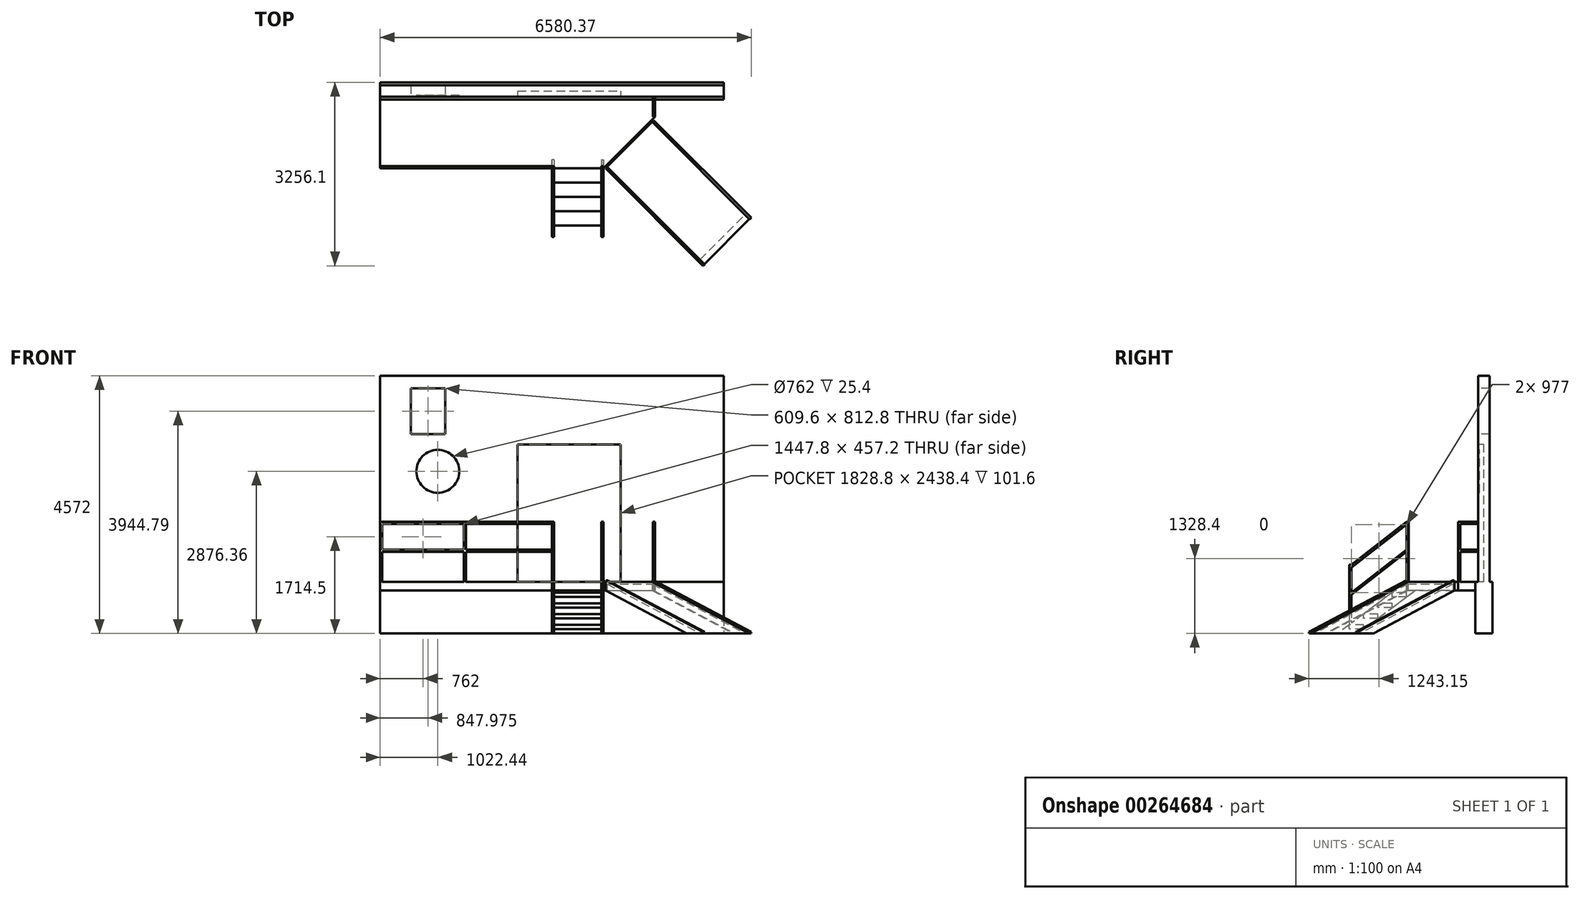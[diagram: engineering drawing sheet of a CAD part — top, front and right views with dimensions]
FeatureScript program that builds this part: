
annotation { "Feature Type Name" : "Feature", "Feature Type Description" : "" }
export const myFeature = defineFeature(function(context is Context, id is Id, definition is map)
    precondition{}
    {
        {
            var Q0;
            Q0=qCreatedBy(makeId("Top.planeOp"),FACE);
            var sketch = newSketch(context, id + "F0", { "sketchPlane" : qUnion([Q0])});
            skLineSegment(sketch, "E0.bottom", {"start": v(-3048, 152.4) * mm, "end": v(3048, 152.4) * mm});
            skLineSegment(sketch, "E0.top", {"start": v(-3048, -152.4) * mm, "end": v(3048, -152.4) * mm});
            skLineSegment(sketch, "E0.left", {"start": v(-3048, 152.4) * mm, "end": v(-3048, -152.4) * mm});
            skLineSegment(sketch, "E0.right", {"start": v(3048, 152.4) * mm, "end": v(3048, -152.4) * mm});
            skPoint(sketch, "E0.middle", {"position": v(0, 0) * mm});
            skSolve(sketch);
        }
        {
            var Q0;
            Q0=makeQuery(id+"F0.imprint","IMPRINT",FACE,{"disambiguationData":[TD([[makeQuery(id+"F0.imprint","IMPRINT",EDGE,{"derivedFrom":sQuery(id+"F0.wireOp",EDGE,"E0.bottom")}),-1.0]])]});
            extrude(context, id + "F1", {"entities" : qUnion([Q0]), "depth" : 914.4 * mm});
        }
        {
            var Q0;
            Q0=qCreatedBy(makeId("Front.planeOp"),FACE);
            var sketch = newSketch(context, id + "F2", { "sketchPlane" : qUnion([Q0])});
            skLineSegment(sketch, "E1.0", {"start": v(-3048, 914.4) * mm, "end": v(3048, 914.4) * mm});
            skLineSegment(sketch, "E2", {"start": v(-3048, 914.4) * mm, "end": v(-3048, 4572) * mm});
            skLineSegment(sketch, "E3", {"start": v(-3048, 4572) * mm, "end": v(3048, 4572) * mm});
            skLineSegment(sketch, "E4", {"start": v(3048, 4572) * mm, "end": v(3048, 914.4) * mm});
            skSolve(sketch);
        }
        {
            var Q0;
            Q0=makeQuery(id+"F2.imprint","IMPRINT",FACE,{"disambiguationData":[TD([[makeQuery(id+"F2.imprint","IMPRINT",EDGE,{"derivedFrom":sQuery(id+"F2.wireOp",EDGE,"E1.0")}),1.0]])]});
            extrude(context, id + "F3", {"entities" : qUnion([Q0]), "operationType" : NewBodyOperationType.ADD, "endBound" : BoundingType.SYMMETRIC, "depth" : 203.2 * mm});
        }
        {
            var Q0;
            Q0=makeQuery(id+"F3.boolean.opBoolean","MERGE",FACE,{"derivedFrom":[makeQuery(id+"F1.opExtrude","SWEPT_FACE",FACE,{"disambiguationData":[OSD([sQuery(id+"F0.wireOp",EDGE,"E0.right")])]}),makeQuery(id+"F3.opExtrude","SWEPT_FACE",FACE,{"disambiguationData":[OSD([sQuery(id+"F2.wireOp",EDGE,"E4")])]})]});
            cPlane(context, id + "F4", {"entities" : qUnion([Q0]), "cplaneType" : CPlaneType.OFFSET, "offset" : 1219.2 * mm, "oppositeDirection" : true, "width" : 152.4 * mm, "height" : 152.4 * mm});
        }
        {
            var Q0;
            Q0=qCreatedBy(id+"F4.planeOp",FACE);
            var sketch = newSketch(context, id + "F5", { "sketchPlane" : qUnion([Q0])});
            skPoint(sketch, "E5.0", {"position": v(-152.4, 914.4) * mm});
            skLineSegment(sketch, "E6.bottom", {"start": v(-152.4, 914.4) * mm, "end": v(-1371.6, 914.4) * mm});
            skLineSegment(sketch, "E6.top", {"start": v(-152.4, 762) * mm, "end": v(-1371.6, 762) * mm});
            skLineSegment(sketch, "E6.left", {"start": v(-152.4, 914.4) * mm, "end": v(-152.4, 762) * mm});
            skLineSegment(sketch, "E6.right", {"start": v(-1371.6, 914.4) * mm, "end": v(-1371.6, 762) * mm});
            skSolve(sketch);
        }
        {
            var Q0;
            Q0=makeQuery(id+"F5.imprint","IMPRINT",FACE,{"disambiguationData":[TD([[makeQuery(id+"F5.imprint","IMPRINT",EDGE,{"derivedFrom":sQuery(id+"F5.wireOp",EDGE,"E6.bottom")}),1.0]])]});
            extrude(context, id + "F6", {"entities" : qUnion([Q0]), "oppositeDirection" : true, "depth" : 4876.8 * mm});
        }
        {
            var Q0;
            Q0=makeQuery(id+"F3.opExtrude","CAP_FACE",FACE,{"disambiguationData":[OSD([sQuery(id+"F2.wireOp",EDGE,"E1.0"),sQuery(id+"F2.wireOp",EDGE,"E2"),sQuery(id+"F2.wireOp",EDGE,"E3"),sQuery(id+"F2.wireOp",EDGE,"E4")])],"isStart":false});
            var sketch = newSketch(context, id + "F7", { "sketchPlane" : qUnion([Q0])});
            skLineSegment(sketch, "E7.bottom", {"start": v(1219.2, 914.4) * mm, "end": v(-609.6, 914.4) * mm});
            skLineSegment(sketch, "E7.top", {"start": v(1219.2, 3352.8) * mm, "end": v(-609.6, 3352.8) * mm});
            skLineSegment(sketch, "E7.left", {"start": v(1219.2, 914.4) * mm, "end": v(1219.2, 3352.8) * mm});
            skLineSegment(sketch, "E7.right", {"start": v(-609.6, 914.4) * mm, "end": v(-609.6, 3352.8) * mm});
            skSolve(sketch);
        }
        {
            var Q0;
            Q0=makeQuery(id+"F7.imprint","IMPRINT",FACE,{"disambiguationData":[TD([[makeQuery(id+"F7.imprint","IMPRINT",EDGE,{"derivedFrom":sQuery(id+"F7.wireOp",EDGE,"E7.bottom")}),1.0]])]});
            extrude(context, id + "F8", {"entities" : qUnion([Q0]), "operationType" : NewBodyOperationType.REMOVE, "oppositeDirection" : true, "depth" : 101.6 * mm});
        }
        {
            var Q0;
            Q0=makeQuery(id+"F6.opExtrude","CAP_EDGE",EDGE,{"disambiguationData":[OSD([sQuery(id+"F5.wireOp",EDGE,"E6.right")])],"isStart":true});
            chamfer(context, id + "F9", {"entities" : qUnion([Q0]), "width" : 914.4 * mm, "tangentPropagation" : true});
        }
        {
            var Q0;
            {var subQ0=sQuery(id+"F5.wireOp",EDGE,"E6.right");Q0=makeQuery(id+"F9.opChamfer","BLEND_EDGE",EDGE,{"blendedFrom":[makeQuery(id+"F6.opExtrude","CAP_EDGE",EDGE,{"disambiguationData":[OSD([subQ0])],"isStart":true}),makeQuery(id+"F6.opExtrude","SWEPT_FACE",FACE,{"disambiguationData":[OSD([subQ0])]})],"blendedInto":[makeQuery(id+"F6.opExtrude","SWEPT_FACE",FACE,{"disambiguationData":[OSD([subQ0])]})]});}
            cPoint(context, id + "F10", {"entities" : qUnion([Q0]), "parameter" : 0.5});
        }
        {
            var Q0;
            Q0=qCreatedBy(id+"F4.planeOp",FACE);
            var Q1;
            Q1 = qCreatedBy(id + "F10" ,VERTEX);
            cPlane(context, id + "F11", {"entities" : qUnion([Q0, Q1]), "cplaneType" : CPlaneType.PLANE_POINT, "offset" : 25.4 * mm, "width" : 152.4 * mm, "height" : 152.4 * mm});
        }
        {
            var Q0;
            Q0=qCreatedBy(id+"F11.planeOp",FACE);
            var sketch = newSketch(context, id + "F12", { "sketchPlane" : qUnion([Q0])});
            skLineSegment(sketch, "E8.0", {"start": v(-1371.6, 914.4) * mm, "end": v(-152.4, 914.4) * mm});
            skLineSegment(sketch, "E9.0", {"start": v(-457.2, 762) * mm, "end": v(-1371.6, 762) * mm});
            skLineSegment(sketch, "E10", {"start": v(-1371.6, 914.4) * mm, "end": v(-2590.8, 0) * mm});
            skLineSegment(sketch, "E11", {"start": v(-2590.8, 0) * mm, "end": v(-2235.2, 0) * mm});
            skLineSegment(sketch, "E12", {"start": v(-2235.2, 0) * mm, "end": v(-1219.2, 762) * mm});
            skLineSegment(sketch, "E13", {"start": v(-1219.2, 762) * mm, "end": v(-1371.6, 762) * mm});
            skLineSegment(sketch, "E14.bottom", {"start": v(-1371.6, 647.7) * mm, "end": v(-1625.6, 647.7) * mm});
            skLineSegment(sketch, "E14.top", {"start": v(-1371.6, 723.9) * mm, "end": v(-1625.6, 723.9) * mm});
            skLineSegment(sketch, "E14.left", {"start": v(-1371.6, 647.7) * mm, "end": v(-1371.6, 723.9) * mm});
            skLineSegment(sketch, "E14.right", {"start": v(-1625.6, 647.7) * mm, "end": v(-1625.6, 723.9) * mm});
            skLineSegment(sketch, "E15.bottom", {"start": v(-1625.6, 457.2) * mm, "end": v(-1879.6, 457.2) * mm});
            skLineSegment(sketch, "E15.top", {"start": v(-1625.6, 533.4) * mm, "end": v(-1879.6, 533.4) * mm});
            skLineSegment(sketch, "E15.left", {"start": v(-1625.6, 457.2) * mm, "end": v(-1625.6, 533.4) * mm});
            skLineSegment(sketch, "E15.right", {"start": v(-1879.6, 457.2) * mm, "end": v(-1879.6, 533.4) * mm});
            skLineSegment(sketch, "E16.bottom", {"start": v(-1879.6, 266.7) * mm, "end": v(-2133.6, 266.7) * mm});
            skLineSegment(sketch, "E16.top", {"start": v(-1879.6, 342.9) * mm, "end": v(-2133.6, 342.9) * mm});
            skLineSegment(sketch, "E16.left", {"start": v(-1879.6, 266.7) * mm, "end": v(-1879.6, 342.9) * mm});
            skLineSegment(sketch, "E16.right", {"start": v(-2133.6, 266.7) * mm, "end": v(-2133.6, 342.9) * mm});
            skLineSegment(sketch, "E17.bottom", {"start": v(-2133.6, 76.2) * mm, "end": v(-2387.6, 76.2) * mm});
            skLineSegment(sketch, "E17.top", {"start": v(-2133.6, 152.4) * mm, "end": v(-2387.6, 152.4) * mm});
            skLineSegment(sketch, "E17.left", {"start": v(-2133.6, 76.2) * mm, "end": v(-2133.6, 152.4) * mm});
            skLineSegment(sketch, "E17.right", {"start": v(-2387.6, 76.2) * mm, "end": v(-2387.6, 152.4) * mm});
            skLineSegment(sketch, "E18", {"start": v(-1371.6, 762) * mm, "end": v(-1219.2, 762) * mm});
            skLineSegment(sketch, "E19", {"start": v(-1371.6, 762) * mm, "end": v(-1371.6, 914.4) * mm});
            skSolve(sketch);
        }
        {
            var Q0;
            {var subQ1=sQuery(id+"F12.wireOp",EDGE,"E11");Q0=makeQuery(id+"F12.imprint","IMPRINT",FACE,{"disambiguationData":[TD([[makeQuery(id+"F12.imprint","IMPRINT",EDGE,{"derivedFrom":subQ1}),1.0]])]});}
            var Q1;
            Q1=makeQuery(id+"F12.imprint","IMPRINT",FACE,{"disambiguationData":[TD([[makeQuery(id+"F12.imprint","IMPRINT",EDGE,{"derivedFrom":sQuery(id+"F12.wireOp",EDGE,"E17.bottom")}),-1.0]])]});
            var Q2;
            {var subQ1=sQuery(id+"F12.wireOp",EDGE,"E16.bottom");Q2=makeQuery(id+"F12.imprint","IMPRINT",FACE,{"disambiguationData":[TD([[makeQuery(id+"F12.imprint","IMPRINT",EDGE,{"derivedFrom":subQ1}),1.0]])]});}
            var Q3;
            Q3=makeQuery(id+"F12.imprint","IMPRINT",FACE,{"disambiguationData":[TD([[makeQuery(id+"F12.imprint","IMPRINT",EDGE,{"derivedFrom":sQuery(id+"F12.wireOp",EDGE,"E16.bottom")}),-1.0]])]});
            var Q4;
            {var subQ1=sQuery(id+"F12.wireOp",EDGE,"E15.bottom");Q4=makeQuery(id+"F12.imprint","IMPRINT",FACE,{"disambiguationData":[TD([[makeQuery(id+"F12.imprint","IMPRINT",EDGE,{"derivedFrom":subQ1}),1.0]])]});}
            var Q5;
            Q5=makeQuery(id+"F12.imprint","IMPRINT",FACE,{"disambiguationData":[TD([[makeQuery(id+"F12.imprint","IMPRINT",EDGE,{"derivedFrom":sQuery(id+"F12.wireOp",EDGE,"E15.bottom")}),-1.0]])]});
            var Q6;
            {var subQ1=sQuery(id+"F12.wireOp",EDGE,"E14.bottom");Q6=makeQuery(id+"F12.imprint","IMPRINT",FACE,{"disambiguationData":[TD([[makeQuery(id+"F12.imprint","IMPRINT",EDGE,{"derivedFrom":subQ1}),1.0]])]});}
            var Q7;
            Q7=makeQuery(id+"F12.imprint","IMPRINT",FACE,{"disambiguationData":[TD([[makeQuery(id+"F12.imprint","IMPRINT",EDGE,{"derivedFrom":sQuery(id+"F12.wireOp",EDGE,"E14.bottom")}),-1.0]])]});
            var Q8;
            {var subQ3=sQuery(id+"F12.wireOp",EDGE,"E14.top");Q8=makeQuery(id+"F12.imprint","IMPRINT",FACE,{"disambiguationData":[TD([[makeQuery(id+"F12.imprint","IMPRINT",EDGE,{"derivedFrom":subQ3}),-1.0]])]});}
            extrude(context, id + "F13", {"entities" : qUnion([Q0, Q1, Q2, Q3, Q4, Q5, Q6, Q7, Q8]), "operationType" : NewBodyOperationType.ADD, "oppositeDirection" : true, "depth" : 38.1 * mm});
        }
        {
            var Q0;
            Q0=makeQuery(id+"F12.imprint","IMPRINT",FACE,{"disambiguationData":[TD([[makeQuery(id+"F12.imprint","IMPRINT",EDGE,{"derivedFrom":sQuery(id+"F12.wireOp",EDGE,"E17.bottom")}),-1.0]])]});
            var Q1;
            Q1=makeQuery(id+"F12.imprint","IMPRINT",FACE,{"disambiguationData":[TD([[makeQuery(id+"F12.imprint","IMPRINT",EDGE,{"derivedFrom":sQuery(id+"F12.wireOp",EDGE,"E16.bottom")}),-1.0]])]});
            var Q2;
            Q2=makeQuery(id+"F12.imprint","IMPRINT",FACE,{"disambiguationData":[TD([[makeQuery(id+"F12.imprint","IMPRINT",EDGE,{"derivedFrom":sQuery(id+"F12.wireOp",EDGE,"E15.bottom")}),-1.0]])]});
            var Q3;
            Q3=makeQuery(id+"F12.imprint","IMPRINT",FACE,{"disambiguationData":[TD([[makeQuery(id+"F12.imprint","IMPRINT",EDGE,{"derivedFrom":sQuery(id+"F12.wireOp",EDGE,"E14.bottom")}),-1.0]])]});
            extrude(context, id + "F14", {"entities" : qUnion([Q0, Q1, Q2, Q3]), "operationType" : NewBodyOperationType.ADD, "oppositeDirection" : true, "depth" : 914.4 * mm});
        }
        {
            var Q0;
            Q0=makeQuery(id+"F14.opExtrude","CAP_FACE",FACE,{"disambiguationData":[OSD([sQuery(id+"F12.wireOp",EDGE,"E14.bottom"),sQuery(id+"F12.wireOp",EDGE,"E14.top"),sQuery(id+"F12.wireOp",EDGE,"E14.left"),sQuery(id+"F12.wireOp",EDGE,"E14.right")])],"isStart":false});
            var sketch = newSketch(context, id + "F15", { "sketchPlane" : qUnion([Q0])});
            skLineSegment(sketch, "E20.0", {"start": v(1371.6, 762) * mm, "end": v(1371.6, 914.4) * mm});
            skLineSegment(sketch, "E21.0", {"start": v(1371.6, 914.4) * mm, "end": v(2590.8, 0) * mm});
            skLineSegment(sketch, "E22.0", {"start": v(2235.2, 0) * mm, "end": v(1219.2, 762) * mm});
            skLineSegment(sketch, "E23.0", {"start": v(2590.8, 0) * mm, "end": v(2235.2, 0) * mm});
            skLineSegment(sketch, "E24.0", {"start": v(457.2, 762) * mm, "end": v(1371.6, 762) * mm});
            skSolve(sketch);
        }
        {
            var Q0;
            {var subQ1=sQuery(id+"F15.wireOp",EDGE,"E20.0");Q0=makeQuery(id+"F15.imprint","IMPRINT",FACE,{"disambiguationData":[TD([[makeQuery(id+"F15.imprint","IMPRINT",EDGE,{"derivedFrom":subQ1}),-1.0]])]});}
            var Q1;
            Q1=makeQuery(id+"F15.imprint","IMPRINT",FACE,{"disambiguationData":[TD([[makeQuery(id+"F15.imprint","IMPRINT",EDGE,{"derivedFrom":makeQuery(id+"F14.opExtrude","CAP_EDGE",EDGE,{"disambiguationData":[OSD([sQuery(id+"F12.wireOp",EDGE,"E14.bottom")])],"isStart":false})}),1.0]])]});
            var Q2;
            {var subQ0=sQuery(id+"F15.wireOp",EDGE,"E23.0");Q2=makeQuery(id+"F15.imprint","IMPRINT",FACE,{"disambiguationData":[TD([[makeQuery(id+"F15.imprint","IMPRINT",EDGE,{"derivedFrom":subQ0}),-1.0]])]});}
            extrude(context, id + "F16", {"entities" : qUnion([Q0, Q1, Q2]), "operationType" : NewBodyOperationType.ADD, "oppositeDirection" : true, "depth" : 38.1 * mm});
        }
        {
            var Q0;
            {var subQ2=sQuery(id+"F0.wireOp",EDGE,"E0.right");var subQ3=sQuery(id+"F0.wireOp",EDGE,"E0.left");var subQ4=sQuery(id+"F0.wireOp",EDGE,"E0.top");Q0=makeQuery(id+"F8.boolean.opBoolean","MERGE",FACE,{"derivedFrom":[makeQuery(id+"F6.boolean.opBoolean","MERGE",FACE,{"derivedFrom":[makeQuery(id+"F3.boolean.opBoolean","SPLIT",FACE,{"disambiguationData":[TD([makeQuery(id+"F1.opExtrude","SWEPT_FACE",FACE,{"disambiguationData":[OSD([subQ4])]})])],"derivedFrom":makeQuery(id+"F1.opExtrude","CAP_FACE",FACE,{"disambiguationData":[OSD([sQuery(id+"F0.wireOp",EDGE,"E0.bottom"),subQ4,subQ3,subQ2])],"isStart":false})}),makeQuery(id+"F6.opExtrude","SWEPT_FACE",FACE,{"disambiguationData":[OSD([sQuery(id+"F5.wireOp",EDGE,"E6.bottom")])]})]}),makeQuery(id+"F8.opExtrude","SWEPT_FACE",FACE,{"disambiguationData":[OSD([sQuery(id+"F7.wireOp",EDGE,"E7.bottom")])]})]});}
            var sketch = newSketch(context, id + "F17", { "sketchPlane" : qUnion([Q0])});
            skLineSegment(sketch, "E25.bottom", {"start": v(-3048, -1371.6) * mm, "end": v(-3009.9, -1371.6) * mm});
            skLineSegment(sketch, "E25.top", {"start": v(-3048, -1333.5) * mm, "end": v(-3009.9, -1333.5) * mm});
            skLineSegment(sketch, "E25.left", {"start": v(-3048, -1371.6) * mm, "end": v(-3048, -1333.5) * mm});
            skLineSegment(sketch, "E25.right", {"start": v(-3009.9, -1371.6) * mm, "end": v(-3009.9, -1333.5) * mm});
            skLineSegment(sketch, "E26.bottom", {"start": v(0, -1371.6) * mm, "end": v(38.1, -1371.6) * mm});
            skLineSegment(sketch, "E26.top", {"start": v(0, -1333.5) * mm, "end": v(38.1, -1333.5) * mm});
            skLineSegment(sketch, "E26.left", {"start": v(0, -1371.6) * mm, "end": v(0, -1333.5) * mm});
            skLineSegment(sketch, "E26.right", {"start": v(38.1, -1371.6) * mm, "end": v(38.1, -1333.5) * mm});
            skLineSegment(sketch, "E27.bottom", {"start": v(914.4, -1371.6) * mm, "end": v(876.3, -1371.6) * mm});
            skLineSegment(sketch, "E27.top", {"start": v(914.4, -1333.5) * mm, "end": v(876.3, -1333.5) * mm});
            skLineSegment(sketch, "E27.left", {"start": v(914.4, -1371.6) * mm, "end": v(914.4, -1333.5) * mm});
            skLineSegment(sketch, "E27.right", {"start": v(876.3, -1371.6) * mm, "end": v(876.3, -1333.5) * mm});
            skLineSegment(sketch, "E28.bottom", {"start": v(1828.8, -457.2) * mm, "end": v(1790.7, -457.2) * mm});
            skLineSegment(sketch, "E28.top", {"start": v(1828.8, -419.1) * mm, "end": v(1790.7, -419.1) * mm});
            skLineSegment(sketch, "E28.left", {"start": v(1828.8, -457.2) * mm, "end": v(1828.8, -419.1) * mm});
            skLineSegment(sketch, "E28.right", {"start": v(1790.7, -457.2) * mm, "end": v(1790.7, -419.1) * mm});
            skLineSegment(sketch, "E29.bottom", {"start": v(-1562.1, -1371.6) * mm, "end": v(-1524, -1371.6) * mm});
            skLineSegment(sketch, "E29.top", {"start": v(-1562.1, -1333.5) * mm, "end": v(-1524, -1333.5) * mm});
            skLineSegment(sketch, "E29.left", {"start": v(-1562.1, -1371.6) * mm, "end": v(-1562.1, -1333.5) * mm});
            skLineSegment(sketch, "E29.right", {"start": v(-1524, -1371.6) * mm, "end": v(-1524, -1333.5) * mm});
            skSolve(sketch);
        }
        {
            var Q0;
            Q0=makeQuery(id+"F17.imprint","IMPRINT",FACE,{"disambiguationData":[TD([[makeQuery(id+"F17.imprint","IMPRINT",EDGE,{"derivedFrom":sQuery(id+"F17.wireOp",EDGE,"E25.bottom")}),1.0]])]});
            var Q1;
            Q1=makeQuery(id+"F17.imprint","IMPRINT",FACE,{"disambiguationData":[TD([[makeQuery(id+"F17.imprint","IMPRINT",EDGE,{"derivedFrom":sQuery(id+"F17.wireOp",EDGE,"E29.bottom")}),1.0]])]});
            var Q2;
            Q2=makeQuery(id+"F17.imprint","IMPRINT",FACE,{"disambiguationData":[TD([[makeQuery(id+"F17.imprint","IMPRINT",EDGE,{"derivedFrom":sQuery(id+"F17.wireOp",EDGE,"E26.bottom")}),-1.0]])]});
            var Q3;
            Q3=makeQuery(id+"F17.imprint","IMPRINT",FACE,{"disambiguationData":[TD([[makeQuery(id+"F17.imprint","IMPRINT",EDGE,{"derivedFrom":sQuery(id+"F17.wireOp",EDGE,"E27.bottom")}),1.0]])]});
            var Q4;
            Q4=makeQuery(id+"F17.imprint","IMPRINT",FACE,{"disambiguationData":[TD([[makeQuery(id+"F17.imprint","IMPRINT",EDGE,{"derivedFrom":sQuery(id+"F17.wireOp",EDGE,"E28.bottom")}),-1.0]])]});
            var Q5;
            Q5=makeQuery(id+"F17.imprint","IMPRINT",FACE,{"disambiguationData":[TD([[makeQuery(id+"F17.imprint","IMPRINT",EDGE,{"derivedFrom":sQuery(id+"F17.wireOp",EDGE,"E26.bottom")}),1.0]])]});
            var Q6;
            Q6=makeQuery(id+"F17.imprint","IMPRINT",FACE,{"disambiguationData":[TD([[makeQuery(id+"F17.imprint","IMPRINT",EDGE,{"derivedFrom":sQuery(id+"F17.wireOp",EDGE,"E27.bottom")}),-1.0]])]});
            extrude(context, id + "F18", {"entities" : qUnion([Q0, Q1, Q2, Q3, Q4, Q5, Q6]), "operationType" : NewBodyOperationType.ADD, "depth" : 1066.8 * mm});
        }
        {
            var Q0;
            Q0=makeQuery(id+"F18.opExtrude","SWEPT_FACE",FACE,{"disambiguationData":[OSD([sQuery(id+"F17.wireOp",EDGE,"E26.left")])]});
            var sketch = newSketch(context, id + "F19", { "sketchPlane" : qUnion([Q0])});
            skLineSegment(sketch, "E30.bottom", {"start": v(1333.5, 1981.2) * mm, "end": v(1371.6, 1981.2) * mm});
            skLineSegment(sketch, "E30.top", {"start": v(1333.5, 1943.1) * mm, "end": v(1371.6, 1943.1) * mm});
            skLineSegment(sketch, "E30.left", {"start": v(1333.5, 1981.2) * mm, "end": v(1333.5, 1943.1) * mm});
            skLineSegment(sketch, "E30.right", {"start": v(1371.6, 1981.2) * mm, "end": v(1371.6, 1943.1) * mm});
            skLineSegment(sketch, "E31.bottom", {"start": v(1371.6, 1447.8) * mm, "end": v(1333.5, 1447.8) * mm});
            skLineSegment(sketch, "E31.top", {"start": v(1371.6, 1485.9) * mm, "end": v(1333.5, 1485.9) * mm});
            skLineSegment(sketch, "E31.left", {"start": v(1371.6, 1447.8) * mm, "end": v(1371.6, 1485.9) * mm});
            skLineSegment(sketch, "E31.right", {"start": v(1333.5, 1447.8) * mm, "end": v(1333.5, 1485.9) * mm});
            skSolve(sketch);
        }
        {
            var Q0;
            Q0=makeQuery(id+"F19.imprint","IMPRINT",FACE,{"disambiguationData":[TD([[makeQuery(id+"F19.imprint","IMPRINT",EDGE,{"derivedFrom":sQuery(id+"F19.wireOp",EDGE,"E30.bottom")}),1.0]])]});
            var Q1;
            Q1=makeQuery(id+"F19.imprint","IMPRINT",FACE,{"disambiguationData":[TD([[makeQuery(id+"F19.imprint","IMPRINT",EDGE,{"derivedFrom":sQuery(id+"F19.wireOp",EDGE,"E31.bottom")}),-1.0]])]});
            var Q2;
            Q2=makeQuery(id+"F18.boolean.opBoolean","MERGE",FACE,{"derivedFrom":[makeQuery(id+"F6.boolean.opBoolean","MERGE",FACE,{"derivedFrom":[makeQuery(id+"F3.boolean.opBoolean","MERGE",FACE,{"derivedFrom":[makeQuery(id+"F1.opExtrude","SWEPT_FACE",FACE,{"disambiguationData":[OSD([sQuery(id+"F0.wireOp",EDGE,"E0.left")])]}),makeQuery(id+"F3.opExtrude","SWEPT_FACE",FACE,{"disambiguationData":[OSD([sQuery(id+"F2.wireOp",EDGE,"E2")])]})]}),makeQuery(id+"F6.opExtrude","CAP_FACE",FACE,{"disambiguationData":[OSD([sQuery(id+"F5.wireOp",EDGE,"E6.bottom"),sQuery(id+"F5.wireOp",EDGE,"E6.top"),sQuery(id+"F5.wireOp",EDGE,"E6.left"),sQuery(id+"F5.wireOp",EDGE,"E6.right")])],"isStart":false})]}),makeQuery(id+"F18.opExtrude","SWEPT_FACE",FACE,{"disambiguationData":[OSD([sQuery(id+"F17.wireOp",EDGE,"E25.left")])]})]});
            extrude(context, id + "F20", {"entities" : qUnion([Q0, Q1]), "operationType" : NewBodyOperationType.ADD, "endBound" : BoundingType.UP_TO_SURFACE, "endBoundEntityFace" : qUnion([Q2]), "depth" : 25.4 * mm});
        }
        {
            var Q0;
            Q0=makeQuery(id+"F18.opExtrude","SWEPT_FACE",FACE,{"disambiguationData":[OSD([sQuery(id+"F17.wireOp",EDGE,"E28.top")])]});
            var sketch = newSketch(context, id + "F21", { "sketchPlane" : qUnion([Q0])});
            skLineSegment(sketch, "E32.bottom", {"start": v(-1828.8, 1981.2) * mm, "end": v(-1790.7, 1981.2) * mm});
            skLineSegment(sketch, "E32.top", {"start": v(-1828.8, 1943.1) * mm, "end": v(-1790.7, 1943.1) * mm});
            skLineSegment(sketch, "E32.left", {"start": v(-1828.8, 1981.2) * mm, "end": v(-1828.8, 1943.1) * mm});
            skLineSegment(sketch, "E32.right", {"start": v(-1790.7, 1981.2) * mm, "end": v(-1790.7, 1943.1) * mm});
            skLineSegment(sketch, "E33.bottom", {"start": v(-1828.8, 1447.8) * mm, "end": v(-1790.7, 1447.8) * mm});
            skLineSegment(sketch, "E33.top", {"start": v(-1828.8, 1485.9) * mm, "end": v(-1790.7, 1485.9) * mm});
            skLineSegment(sketch, "E33.left", {"start": v(-1828.8, 1447.8) * mm, "end": v(-1828.8, 1485.9) * mm});
            skLineSegment(sketch, "E33.right", {"start": v(-1790.7, 1447.8) * mm, "end": v(-1790.7, 1485.9) * mm});
            skSolve(sketch);
        }
        {
            var Q0;
            Q0=makeQuery(id+"F21.imprint","IMPRINT",FACE,{"disambiguationData":[TD([[makeQuery(id+"F21.imprint","IMPRINT",EDGE,{"derivedFrom":sQuery(id+"F21.wireOp",EDGE,"E32.bottom")}),-1.0]])]});
            var Q1;
            Q1=makeQuery(id+"F21.imprint","IMPRINT",FACE,{"disambiguationData":[TD([[makeQuery(id+"F21.imprint","IMPRINT",EDGE,{"derivedFrom":sQuery(id+"F21.wireOp",EDGE,"E33.bottom")}),1.0]])]});
            extrude(context, id + "F22", {"entities" : qUnion([Q0, Q1]), "operationType" : NewBodyOperationType.ADD, "depth" : 304.8 * mm});
        }
        {
            var Q0;
            Q0=makeQuery(id+"F14.opExtrude","SWEPT_FACE",FACE,{"disambiguationData":[OSD([sQuery(id+"F12.wireOp",EDGE,"E17.top")])]});
            var sketch = newSketch(context, id + "F23", { "sketchPlane" : qUnion([Q0])});
            skLineSegment(sketch, "E34.bottom", {"start": v(38.1, -2387.6) * mm, "end": v(0, -2387.6) * mm});
            skLineSegment(sketch, "E34.top", {"start": v(38.1, -2349.5) * mm, "end": v(0, -2349.5) * mm});
            skLineSegment(sketch, "E34.left", {"start": v(38.1, -2387.6) * mm, "end": v(38.1, -2349.5) * mm});
            skLineSegment(sketch, "E34.right", {"start": v(0, -2387.6) * mm, "end": v(0, -2349.5) * mm});
            skLineSegment(sketch, "E35.bottom", {"start": v(876.3, -2387.6) * mm, "end": v(914.4, -2387.6) * mm});
            skLineSegment(sketch, "E35.top", {"start": v(876.3, -2349.5) * mm, "end": v(914.4, -2349.5) * mm});
            skLineSegment(sketch, "E35.left", {"start": v(876.3, -2387.6) * mm, "end": v(876.3, -2349.5) * mm});
            skLineSegment(sketch, "E35.right", {"start": v(914.4, -2387.6) * mm, "end": v(914.4, -2349.5) * mm});
            skSolve(sketch);
        }
        {
            var Q0;
            Q0=makeQuery(id+"F23.imprint","IMPRINT",FACE,{"disambiguationData":[TD([[makeQuery(id+"F23.imprint","IMPRINT",EDGE,{"derivedFrom":sQuery(id+"F23.wireOp",EDGE,"E34.bottom")}),-1.0]])]});
            var Q1;
            Q1=makeQuery(id+"F23.imprint","IMPRINT",FACE,{"disambiguationData":[TD([[makeQuery(id+"F23.imprint","IMPRINT",EDGE,{"derivedFrom":sQuery(id+"F23.wireOp",EDGE,"E35.bottom")}),1.0]])]});
            extrude(context, id + "F24", {"entities" : qUnion([Q0, Q1]), "operationType" : NewBodyOperationType.ADD, "depth" : 1066.8 * mm});
        }
        {
            var Q0;
            Q0=makeQuery(id+"F24.boolean.opBoolean","MERGE",FACE,{"derivedFrom":[makeQuery(id+"F16.boolean.opBoolean","MERGE",FACE,{"derivedFrom":[makeQuery(id+"F14.opExtrude","CAP_FACE",FACE,{"disambiguationData":[OSD([sQuery(id+"F12.wireOp",EDGE,"E14.bottom"),sQuery(id+"F12.wireOp",EDGE,"E14.top"),sQuery(id+"F12.wireOp",EDGE,"E14.left"),sQuery(id+"F12.wireOp",EDGE,"E14.right")])],"isStart":false}),makeQuery(id+"F14.opExtrude","CAP_FACE",FACE,{"disambiguationData":[OSD([sQuery(id+"F12.wireOp",EDGE,"E15.bottom"),sQuery(id+"F12.wireOp",EDGE,"E15.top"),sQuery(id+"F12.wireOp",EDGE,"E15.left"),sQuery(id+"F12.wireOp",EDGE,"E15.right")])],"isStart":false}),makeQuery(id+"F14.opExtrude","CAP_FACE",FACE,{"disambiguationData":[OSD([sQuery(id+"F12.wireOp",EDGE,"E16.bottom"),sQuery(id+"F12.wireOp",EDGE,"E16.top"),sQuery(id+"F12.wireOp",EDGE,"E16.left"),sQuery(id+"F12.wireOp",EDGE,"E16.right")])],"isStart":false}),makeQuery(id+"F14.opExtrude","CAP_FACE",FACE,{"disambiguationData":[OSD([sQuery(id+"F12.wireOp",EDGE,"E17.bottom"),sQuery(id+"F12.wireOp",EDGE,"E17.top"),sQuery(id+"F12.wireOp",EDGE,"E17.left"),sQuery(id+"F12.wireOp",EDGE,"E17.right")])],"isStart":false}),makeQuery(id+"F16.opExtrude","CAP_FACE",FACE,{"disambiguationData":[OSD([sQuery(id+"F15.wireOp",EDGE,"E20.0"),sQuery(id+"F15.wireOp",EDGE,"E21.0"),sQuery(id+"F15.wireOp",EDGE,"E22.0"),sQuery(id+"F15.wireOp",EDGE,"E23.0"),sQuery(id+"F15.wireOp",EDGE,"E24.0")])],"isStart":true})]}),makeQuery(id+"F24.opExtrude","SWEPT_FACE",FACE,{"disambiguationData":[OSD([sQuery(id+"F23.wireOp",EDGE,"E34.right")])]})]});
            var sketch = newSketch(context, id + "F25", { "sketchPlane" : qUnion([Q0])});
            skPoint(sketch, "E36.0", {"position": v(1371.6, 1981.2) * mm});
            skLineSegment(sketch, "E37.0", {"start": v(1371.6, 1981.2) * mm, "end": v(1371.6, 762) * mm});
            skLineSegment(sketch, "E38.0", {"start": v(2349.5, 1219.2) * mm, "end": v(2349.5, 180.98) * mm});
            skLineSegment(sketch, "E39", {"start": v(2349.5, 1219.2) * mm, "end": v(1371.6, 1981.2) * mm});
            skLineSegment(sketch, "E40", {"start": v(2349.5, 1170.9) * mm, "end": v(1371.6, 1932.9) * mm});
            skPoint(sketch, "E41.0", {"position": v(1371.6, 1485.9) * mm});
            skPoint(sketch, "E42.0", {"position": v(1371.6, 1447.8) * mm});
            skLineSegment(sketch, "E43", {"start": v(1371.6, 1485.9) * mm, "end": v(2349.5, 723.9) * mm});
            skLineSegment(sketch, "E44", {"start": v(1371.6, 1447.8) * mm, "end": v(2349.5, 685.8) * mm});
            skLineSegment(sketch, "E45", {"start": v(2349.5, 685.8) * mm, "end": v(2349.5, 723.9) * mm});
            skSolve(sketch);
        }
        {
            var Q0;
            {var subQ0=sQuery(id+"F25.wireOp",EDGE,"E39");Q0=makeQuery(id+"F25.imprint","IMPRINT",FACE,{"disambiguationData":[TD([[makeQuery(id+"F25.imprint","IMPRINT",EDGE,{"derivedFrom":subQ0}),1.0]])]});}
            var Q1;
            {var subQ0=sQuery(id+"F25.wireOp",EDGE,"E43");Q1=makeQuery(id+"F25.imprint","IMPRINT",FACE,{"disambiguationData":[TD([[makeQuery(id+"F25.imprint","IMPRINT",EDGE,{"derivedFrom":subQ0}),-1.0]])]});}
            extrude(context, id + "F26", {"entities" : qUnion([Q0, Q1]), "operationType" : NewBodyOperationType.ADD, "oppositeDirection" : true, "depth" : 38.1 * mm});
        }
        {
            var Q0;
            Q0=makeQuery(id+"F18.opExtrude","SWEPT_FACE",FACE,{"disambiguationData":[OSD([sQuery(id+"F17.wireOp",EDGE,"E27.left")])]});
            var sketch = newSketch(context, id + "F27", { "sketchPlane" : qUnion([Q0])});
            skLineSegment(sketch, "E46.0", {"start": v(-2349.5, 1219.2) * mm, "end": v(-1371.6, 1981.2) * mm});
            skLineSegment(sketch, "E47.0", {"start": v(-2349.5, 1170.9) * mm, "end": v(-1371.6, 1932.9) * mm});
            skLineSegment(sketch, "E48.0", {"start": v(-1371.6, 1485.9) * mm, "end": v(-2349.5, 723.9) * mm});
            skLineSegment(sketch, "E49.0", {"start": v(-1371.6, 1447.8) * mm, "end": v(-2349.5, 685.8) * mm});
            skLineSegment(sketch, "E50.0", {"start": v(-2349.5, 1219.2) * mm, "end": v(-2349.5, 180.98) * mm});
            skLineSegment(sketch, "E51.0", {"start": v(-1371.6, 1981.2) * mm, "end": v(-1371.6, 914.4) * mm});
            skSolve(sketch);
        }
        {
            var Q0;
            {var subQ0=sQuery(id+"F27.wireOp",EDGE,"E46.0");Q0=makeQuery(id+"F27.imprint","IMPRINT",FACE,{"disambiguationData":[TD([[makeQuery(id+"F27.imprint","IMPRINT",EDGE,{"derivedFrom":subQ0}),-1.0]])]});}
            var Q1;
            {var subQ0=sQuery(id+"F27.wireOp",EDGE,"E48.0");Q1=makeQuery(id+"F27.imprint","IMPRINT",FACE,{"disambiguationData":[TD([[makeQuery(id+"F27.imprint","IMPRINT",EDGE,{"derivedFrom":subQ0}),1.0]])]});}
            extrude(context, id + "F28", {"entities" : qUnion([Q0, Q1]), "operationType" : NewBodyOperationType.ADD, "oppositeDirection" : true, "depth" : 38.1 * mm});
        }
        {
            var Q0;
            {var subQ0=sQuery(id+"F5.wireOp",EDGE,"E6.right");Q0=makeQuery(id+"F9.opChamfer","BLEND_EDGE",EDGE,{"blendedFrom":[makeQuery(id+"F6.opExtrude","CAP_EDGE",EDGE,{"disambiguationData":[OSD([subQ0])],"isStart":true}),makeQuery(id+"F6.opExtrude","CAP_FACE",FACE,{"disambiguationData":[OSD([sQuery(id+"F5.wireOp",EDGE,"E6.bottom"),sQuery(id+"F5.wireOp",EDGE,"E6.top"),sQuery(id+"F5.wireOp",EDGE,"E6.left"),subQ0])],"isStart":true})],"blendedInto":[makeQuery(id+"F6.opExtrude","CAP_FACE",FACE,{"disambiguationData":[OSD([sQuery(id+"F5.wireOp",EDGE,"E6.bottom"),sQuery(id+"F5.wireOp",EDGE,"E6.top"),sQuery(id+"F5.wireOp",EDGE,"E6.left"),subQ0])],"isStart":true})]});}
            cPlane(context, id + "F29", {"entities" : qUnion([Q0]), "cplaneType" : CPlaneType.LINE_ANGLE, "offset" : 25.4 * mm, "angle" : 135 * degree, "width" : 152.4 * mm, "height" : 152.4 * mm});
        }
        {
            var Q0;
            Q0=qCreatedBy(id+"F29.planeOp",FACE);
            cPlane(context, id + "F30", {"entities" : qUnion([Q0]), "cplaneType" : CPlaneType.OFFSET, "offset" : 63.5 * mm, "oppositeDirection" : true, "width" : 152.4 * mm, "height" : 152.4 * mm});
        }
        {
            var Q0;
            Q0=qCreatedBy(id+"F30.planeOp",FACE);
            var sketch = newSketch(context, id + "F31", { "sketchPlane" : qUnion([Q0])});
            skLineSegment(sketch, "E52.0", {"start": v(-1616.45, 762) * mm, "end": v(-1616.45, 914.4) * mm});
            skLineSegment(sketch, "E53", {"start": v(-1641.85, 914.4) * mm, "end": v(-1641.85, 762) * mm});
            skLineSegment(sketch, "E54", {"start": v(-1641.85, 762) * mm, "end": v(-3673.85, 0) * mm});
            skLineSegment(sketch, "E55", {"start": v(-3673.85, 0) * mm, "end": v(-4080.25, 0) * mm});
            skLineSegment(sketch, "E56", {"start": v(-4080.25, 0) * mm, "end": v(-1641.85, 914.4) * mm});
            skSolve(sketch);
        }
        {
            var Q0;
            Q0=makeQuery(id+"F31.imprint","IMPRINT",FACE,{"disambiguationData":[TD([[makeQuery(id+"F31.imprint","IMPRINT",EDGE,{"derivedFrom":sQuery(id+"F31.wireOp",EDGE,"E53")}),-1.0]])]});
            extrude(context, id + "F32", {"entities" : qUnion([Q0]), "oppositeDirection" : true, "depth" : 38.1 * mm});
        }
        {
            var Q0;
            Q0=makeQuery(id+"F32.opExtrude","CAP_FACE",FACE,{"disambiguationData":[OSD([sQuery(id+"F31.wireOp",EDGE,"E53"),sQuery(id+"F31.wireOp",EDGE,"E54"),sQuery(id+"F31.wireOp",EDGE,"E55"),sQuery(id+"F31.wireOp",EDGE,"E56")])],"isStart":false});
            var sketch = newSketch(context, id + "F33", { "sketchPlane" : qUnion([Q0])});
            skLineSegment(sketch, "E57", {"start": v(1641.85, 873.7) * mm, "end": v(3971.74, 0) * mm});
            skLineSegment(sketch, "E58.0", {"start": v(4080.25, 0) * mm, "end": v(1641.85, 914.4) * mm});
            skLineSegment(sketch, "E59.0", {"start": v(1641.85, 914.4) * mm, "end": v(1641.85, 762) * mm});
            skLineSegment(sketch, "E60.0", {"start": v(3673.85, 0) * mm, "end": v(4080.25, 0) * mm});
            skSolve(sketch);
        }
        {
            var Q0;
            Q0=makeQuery(id+"F32.opExtrude","SWEPT_FACE",FACE,{"disambiguationData":[OSD([sQuery(id+"F31.wireOp",EDGE,"E56")])]});
            extrude(context, id + "F34", {"entities" : qUnion([Q0]), "operationType" : NewBodyOperationType.ADD, "depth" : 25.4 * mm});
        }
        {
            var Q0;
            {var subQ0=sQuery(id+"F33.wireOp",EDGE,"E57");Q0=makeQuery(id+"F33.imprint","IMPRINT",FACE,{"disambiguationData":[TD([[makeQuery(id+"F33.imprint","IMPRINT",EDGE,{"derivedFrom":subQ0}),1.0]])]});}
            extrude(context, id + "F35", {"entities" : qUnion([Q0]), "operationType" : NewBodyOperationType.ADD, "depth" : 1168.4 * mm});
        }
        {
            var Q0;
            Q0=makeQuery(id+"F35.opExtrude","CAP_FACE",FACE,{"disambiguationData":[OSD([sQuery(id+"F33.wireOp",EDGE,"E57"),sQuery(id+"F33.wireOp",EDGE,"E58.0"),sQuery(id+"F33.wireOp",EDGE,"E59.0"),sQuery(id+"F33.wireOp",EDGE,"E60.0")])],"isStart":false});
            var sketch = newSketch(context, id + "F36", { "sketchPlane" : qUnion([Q0])});
            skLineSegment(sketch, "E61.0", {"start": v(4089.16, 23.78) * mm, "end": v(1650.76, 938.18) * mm});
            skLineSegment(sketch, "E62.0", {"start": v(1650.76, 938.18) * mm, "end": v(1641.85, 914.4) * mm});
            skLineSegment(sketch, "E63.0", {"start": v(1641.85, 914.4) * mm, "end": v(1641.85, 873.7) * mm});
            skLineSegment(sketch, "E64.0", {"start": v(1641.85, 873.7) * mm, "end": v(1641.85, 762) * mm});
            skLineSegment(sketch, "E65.0", {"start": v(1641.85, 762) * mm, "end": v(3673.85, 0) * mm});
            skLineSegment(sketch, "E66.0", {"start": v(3673.85, 0) * mm, "end": v(3971.74, 0) * mm});
            skLineSegment(sketch, "E67.0", {"start": v(3971.74, 0) * mm, "end": v(4080.25, 0) * mm});
            skLineSegment(sketch, "E68.0", {"start": v(4089.16, 23.78) * mm, "end": v(4080.25, 0) * mm});
            skSolve(sketch);
        }
        {
            var Q0;
            Q0=makeQuery(id+"F36.imprint","IMPRINT",FACE,{"disambiguationData":[TD([[makeQuery(id+"F36.imprint","IMPRINT",EDGE,{"derivedFrom":sQuery(id+"F36.wireOp",EDGE,"E64.0")}),1.0]])]});
            var Q1;
            Q1=makeQuery(id+"F36.imprint","IMPRINT",FACE,{"disambiguationData":[TD([[makeQuery(id+"F36.imprint","IMPRINT",EDGE,{"derivedFrom":sQuery(id+"F36.wireOp",EDGE,"E63.0")}),1.0]])]});
            var Q2;
            Q2=makeQuery(id+"F36.imprint","IMPRINT",FACE,{"disambiguationData":[TD([[makeQuery(id+"F36.imprint","IMPRINT",EDGE,{"derivedFrom":sQuery(id+"F36.wireOp",EDGE,"E61.0")}),1.0]])]});
            extrude(context, id + "F37", {"entities" : qUnion([Q0, Q1, Q2]), "operationType" : NewBodyOperationType.ADD, "oppositeDirection" : true, "depth" : 38.1 * mm});
        }
        {
            var Q0;
            Q0=makeQuery(id+"F3.opExtrude","CAP_FACE",FACE,{"disambiguationData":[OSD([sQuery(id+"F2.wireOp",EDGE,"E1.0"),sQuery(id+"F2.wireOp",EDGE,"E2"),sQuery(id+"F2.wireOp",EDGE,"E3"),sQuery(id+"F2.wireOp",EDGE,"E4")])],"isStart":false});
            var sketch = newSketch(context, id + "F38", { "sketchPlane" : qUnion([Q0])});
            skCircle(sketch, "E69", {"center": v(-2025.56, 2876.36) * mm, "radius": 381 * mm});
            skSolve(sketch);
        }
        {
            var Q0;
            Q0=makeQuery(id+"F38.imprint","IMPRINT",FACE,{"disambiguationData":[TD([[makeQuery(id+"F38.imprint","IMPRINT",EDGE,{"derivedFrom":sQuery(id+"F38.wireOp",EDGE,"E69")}),1.0]])]});
            extrude(context, id + "F39", {"entities" : qUnion([Q0]), "operationType" : NewBodyOperationType.REMOVE, "oppositeDirection" : true, "depth" : 25.4 * mm});
        }
        {
            var Q0;
            Q0=makeQuery(id+"F3.opExtrude","CAP_FACE",FACE,{"disambiguationData":[OSD([sQuery(id+"F2.wireOp",EDGE,"E1.0"),sQuery(id+"F2.wireOp",EDGE,"E2"),sQuery(id+"F2.wireOp",EDGE,"E3"),sQuery(id+"F2.wireOp",EDGE,"E4")])],"isStart":false});
            var sketch = newSketch(context, id + "F40", { "sketchPlane" : qUnion([Q0])});
            skLineSegment(sketch, "E70.bottom", {"start": v(-1895.23, 4351.19) * mm, "end": v(-2504.83, 4351.19) * mm});
            skLineSegment(sketch, "E70.top", {"start": v(-1895.23, 3538.39) * mm, "end": v(-2504.83, 3538.39) * mm});
            skLineSegment(sketch, "E70.left", {"start": v(-1895.23, 4351.19) * mm, "end": v(-1895.23, 3538.39) * mm});
            skLineSegment(sketch, "E70.right", {"start": v(-2504.83, 4351.19) * mm, "end": v(-2504.83, 3538.39) * mm});
            skSolve(sketch);
        }
        {
            var Q0;
            Q0=makeQuery(id+"F40.imprint","IMPRINT",FACE,{"disambiguationData":[TD([[makeQuery(id+"F40.imprint","IMPRINT",EDGE,{"derivedFrom":sQuery(id+"F40.wireOp",EDGE,"E70.bottom")}),1.0]])]});
            extrude(context, id + "F41", {"entities" : qUnion([Q0]), "operationType" : NewBodyOperationType.REMOVE, "endBound" : BoundingType.THROUGH_ALL, "oppositeDirection" : true, "depth" : 25.4 * mm});
        }
    });
